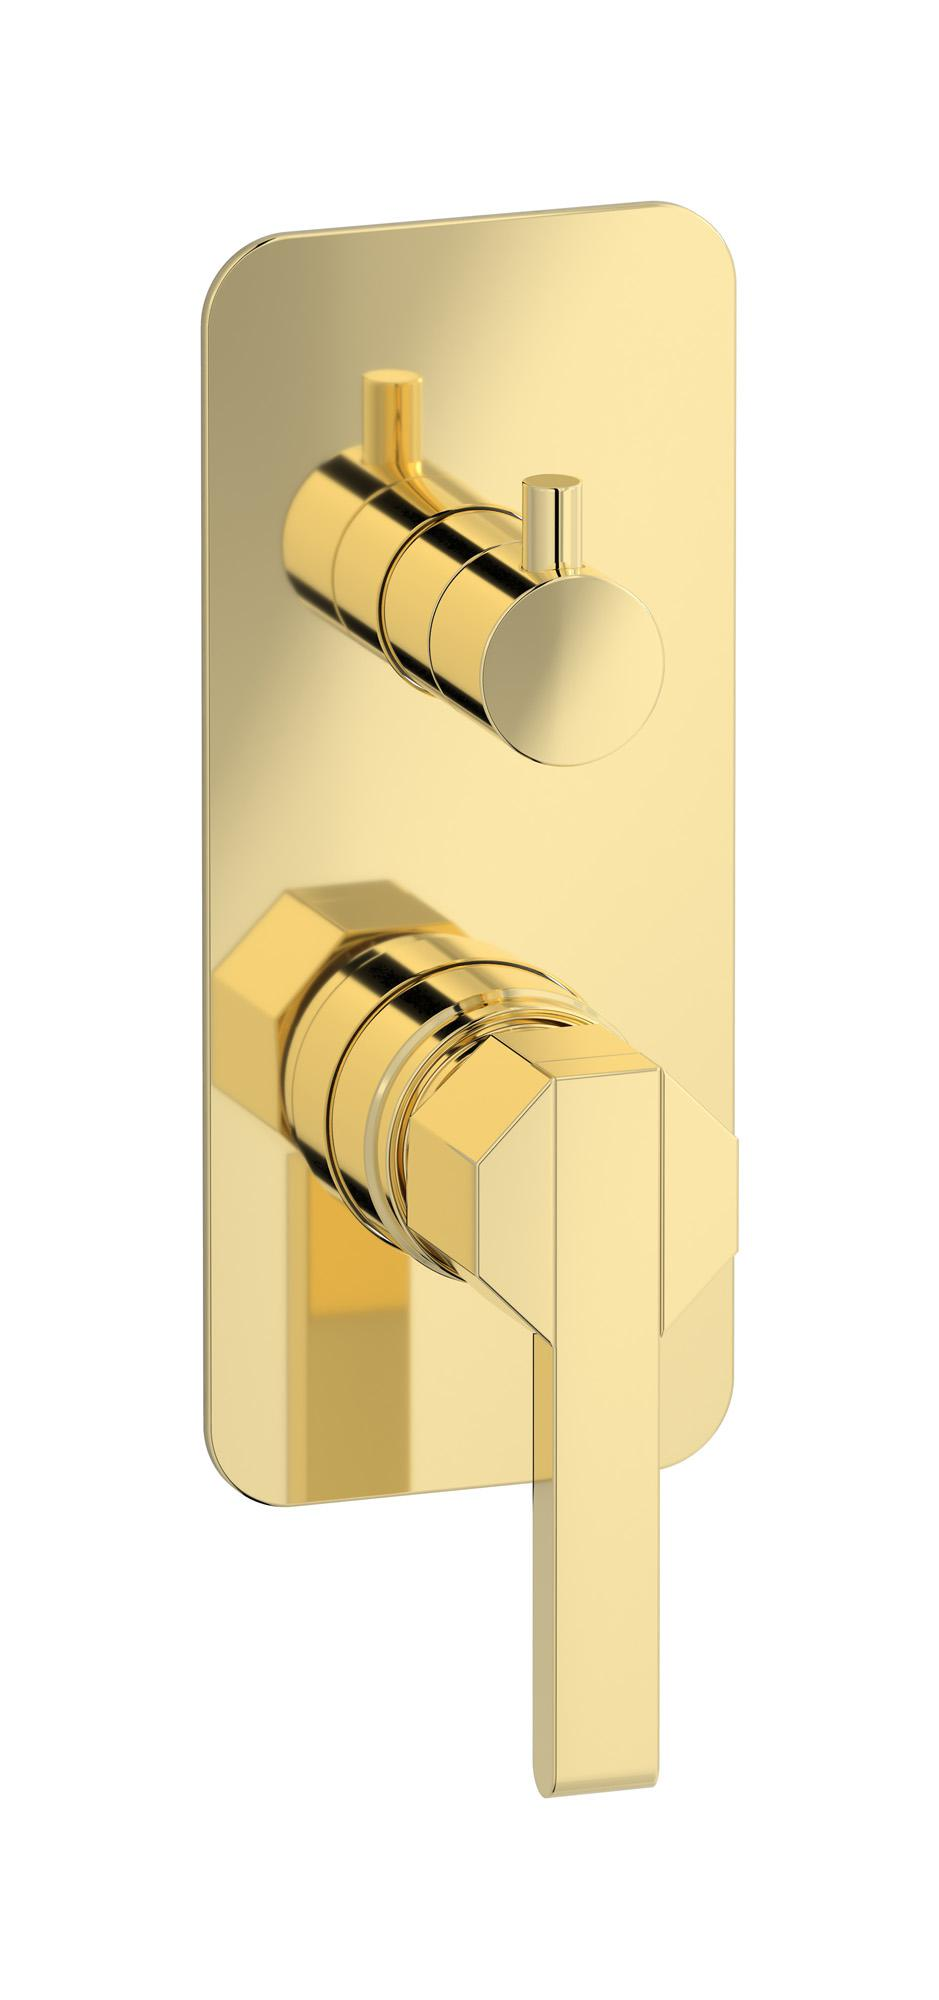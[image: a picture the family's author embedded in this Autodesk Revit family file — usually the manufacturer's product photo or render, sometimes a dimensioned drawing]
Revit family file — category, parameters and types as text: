
# Revit family: BL312
name_source: partatom
category: Apparecchi idraulici
units: mm (PartAtom-declared; Revit-internal decimal feet)

## family parameters
Basato su piano di lavoro = No
Condiviso = No
Mantieni orientamento annotazione = No
Numero OmniClass = 23.45.55.17
Punto di calcolo locali = No
Quota connettore circolare = Usa diametro
Sempre verticale = Sì
Taglio con vuoti quando caricato = No
Tipo di parte = Normale
Titolo OmniClass = Mixing Faucets

## types (7) — shared parameters
Cold water inlet = 10 mm  [stored 0.0328084 ft]
Commenti sul tipo = Wall mixer
Connessione CW = No
Connessione HW = No
Connessione di scarico = No
Connessione di ventilazione = No
Descrizione = Exposed parts for manual wall mixer with three ways diverter
Hot water inlet = 10 mm  [stored 0.0328084 ft]
Produttore = IB Rubinetterie S.p.A.
URL = https://www.weareib.it
zero-valued in all types: Prospetto di default

## per-type parameters (varying)
| type | Finishes surface | Immagine tipo | Modello |
| Chrome | IB_Chrome | BL312CC.jpg | BL312CC |
| Gold | IB_gold | BL312OO.jpg | BL312OO |
| Rose gold | IB_Rose gold | BL312RS.jpg | BL312RS |
| Platinum | IB_Platinum | BL312PL.jpg | BL312PL |
| Pale gold | IB_Pale gold | BL312II.jpg | BL312II |
| Modern Bronze | IB_Modern bronze | BL312MB.jpg | BL312MB |
| Brushed Nickel | IB_Brushed nickel | BL312SS.jpg | BL312SS |

note: [stored X ft] marks values corroborated as IEEE doubles in the binary element streams (Revit-internal decimal feet)
